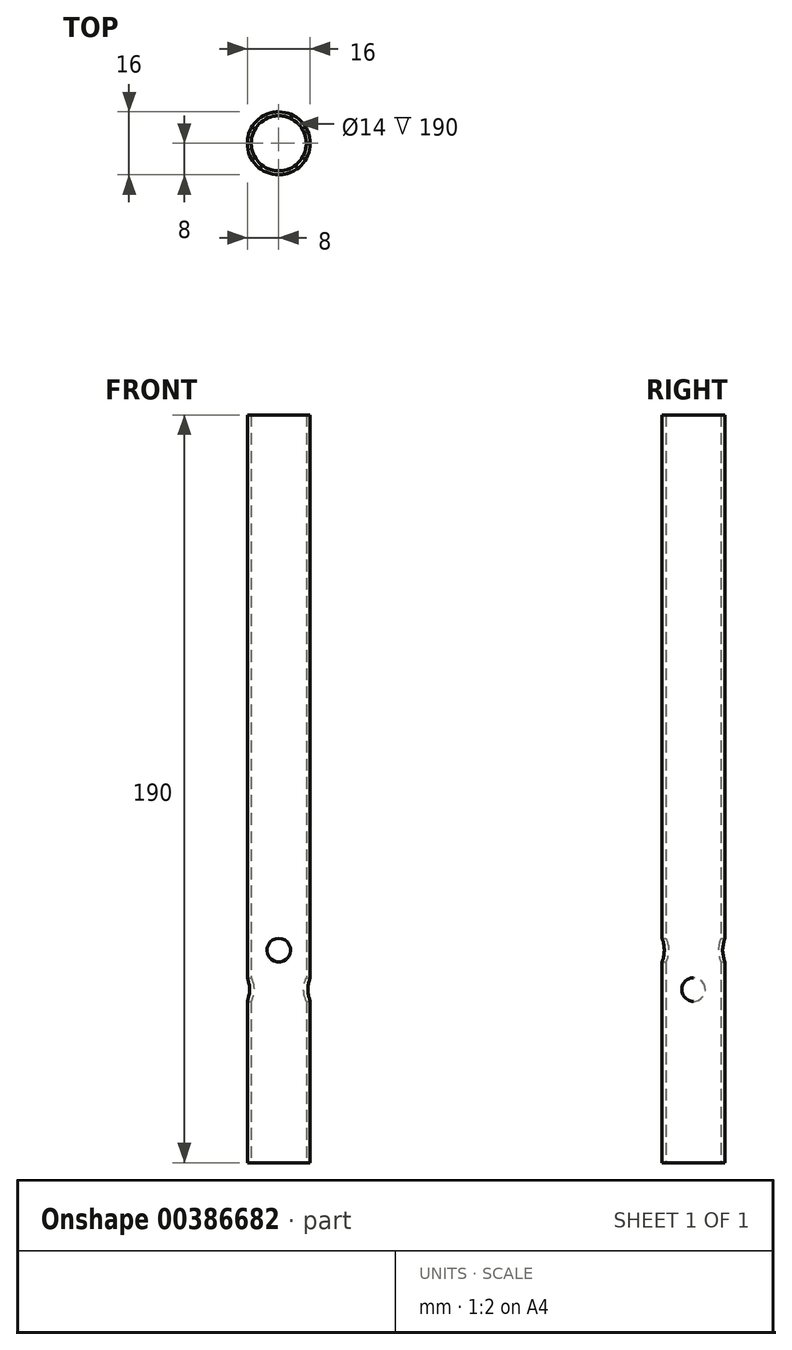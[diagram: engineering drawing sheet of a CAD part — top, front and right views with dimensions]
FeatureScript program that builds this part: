
annotation { "Feature Type Name" : "Feature", "Feature Type Description" : "" }
export const myFeature = defineFeature(function(context is Context, id is Id, definition is map)
    precondition{}
    {
        {
            var Q0;
            Q0=qCreatedBy(makeId("Top.planeOp"),FACE);
            var sketch = newSketch(context, id + "F0", { "sketchPlane" : qUnion([Q0])});
            skCircle(sketch, "E0", {"center": v(0, 0) * mm, "radius": 8 * mm});
            skCircle(sketch, "E1", {"center": v(0, 0) * mm, "radius": 7 * mm});
            skSolve(sketch);
        }
        {
            var Q0;
            Q0 = qSketchRegion(id + "F0", true);
            extrude(context, id + "F1", {"entities" : qUnion([Q0]), "depth" : 190 * mm});
        }
        {
            var Q0;
            Q0=qCreatedBy(makeId("Right.planeOp"),FACE);
            var sketch = newSketch(context, id + "F2", { "sketchPlane" : qUnion([Q0])});
            skCircle(sketch, "E2", {"center": v(0, 44) * mm, "radius": 3 * mm});
            skSolve(sketch);
        }
        {
            var Q0;
            Q0 = qSketchRegion(id + "F2", true);
            extrude(context, id + "F3", {"entities" : qUnion([Q0]), "operationType" : NewBodyOperationType.REMOVE, "endBound" : BoundingType.SYMMETRIC, "oppositeDirection" : true, "depth" : 40 * mm});
        }
        {
            var Q0;
            Q0=qCreatedBy(makeId("Front.planeOp"),FACE);
            var sketch = newSketch(context, id + "F4", { "sketchPlane" : qUnion([Q0])});
            skCircle(sketch, "E3", {"center": v(0, 54) * mm, "radius": 3 * mm});
            skSolve(sketch);
        }
        {
            var Q0;
            Q0 = qSketchRegion(id + "F4", true);
            extrude(context, id + "F5", {"entities" : qUnion([Q0]), "operationType" : NewBodyOperationType.REMOVE, "endBound" : BoundingType.SYMMETRIC, "depth" : 25 * mm});
        }
    });
